# Revit family: Windows_Roof-Windows_FAKRO_Deck-mounted-roof-access window-FWU-G3
name_source: partatom
category: Okna
revit_build: Autodesk Revit 2015 (Build: 20140606_1530(x64)
units: mm (PartAtom-declared; Revit-internal decimal feet)

## types (2) — shared parameters
Actuator R1 = Nie
Actuator R2 = Nie
Apron Material = Aluminium - FAKRO - RAL7022
Bimobject Category = Windows - Roof Windows
CSI MasterFormat 2016 Code = 08 60 00
CSI MasterFormat 2016 Title = Roof Windows and Skylights
Colour = Natural-pine
Glazing = Glass - FAKRO
Glazing unit = 4H-16-4T
Handle Material = Handle - FAKRO - RAL9003
Hidden = Nie
IFC Classification = Window
Installation instructions = https://www.fakrousa.com
Kod zespołu = B3020110
Left sash = Tak
Material = Pinewood
Material Actuators = Aluminium - FAKRO - RAL9006
Material External = Aluminium - FAKRO - RAL7022
Material Internal = Pinewood - FAKRO - Frame
Material main = Wood
Material secondary = Glass
Model = FWU G3
Mounting anchors = Tak
OmniClass Code = 21-02 03 06 01
OmniClass Description = Roof Windows and Skylights
Open window = Nie
Opening method = Opened to the left (FWU-L) or opened to the right (FWU-R)
Operation mode = Manual
Opis = Deck mounted roof access window
Parameter A = 0.00°
Parameter B = 20 3/4"
Parameter C = 11 1/4"
Producent = FAKRO
Product url = https://www.fakrousa.com
Right sash = Nie
Roof angle = 15-55°
Seal Material = Rubber - FAKRO
Solar Heat Gain Coefficient (NFRC 200) = 0.2
Szerokość = 23 1/2"
Szerokość brutto = 0"
Technical description = https://www.fakrousa.com
UNSPC Category = Roofing accessories
UNSPC Code = 301516
URL = www.fakrousa.com
Uniformat II Code = B3060,10
Uniformat II Description = Roof Windows and Skylights
Visible Transmittance (NFRC 200) = 0.37
Warning = The present model is for informational-demonstrative purposes only and as such cannot constitute a basis for performance. All dimensions presented in this model should be verified on site. Because of the fact that the model is a schematic one, FAKRO shall not assume any responsibility for the actual installation quality on the roof.
Window acoustic performance Rw [dB] = 34
Wysokość brutto = 0"
Youtube clip = https://www.fakrousa.com

## per-type parameters (varying)
| type | Actuator L1 | Actuator L2 | Glass perimeter ["] | Obj Type | Parameter D | Weight Net (Kg) | Weight Net (lbs) | Window perimeter ["] | Wysokość |
| FWU G3 24x38 | Tak | Nie | 101 5/8" | 1 | 16 3/8" | 25 | 55 | 123 1/4" | 38 1/8" |
| FWU G3 24x46 | Nie | Tak | 117 7/8" | 2 | 22 3/8" | 28 | 62 | 139 1/2" | 46 1/4" |

## geometry (parser evidence)
native form markers: Sweep x3
no freeform markers — native parametric forms only
